annotation { "Feature Type Name" : "Feature", "Feature Type Description" : "" }
export const myFeature = defineFeature(function(context is Context, id is Id, definition is map)
    precondition{}
    {
        {
            var Q0;
            Q0=qCreatedBy(makeId("Front.planeOp"),FACE);
            var sketch = newSketch(context, id + "F0", { "sketchPlane" : qUnion([Q0])});
            skLineSegment(sketch, "E0.bottom", {"start": v(0, 0) * mm, "end": v(12.7, 0) * mm, "construction": true});
            skLineSegment(sketch, "E0.top", {"start": v(0, 38.1) * mm, "end": v(12.7, 38.1) * mm, "construction": true});
            skLineSegment(sketch, "E0.left", {"start": v(0, 0) * mm, "end": v(0, 38.1) * mm, "construction": true});
            skLineSegment(sketch, "E0.right", {"start": v(12.7, 0) * mm, "end": v(12.7, 38.1) * mm, "construction": true});
            skLineSegment(sketch, "E1", {"start": v(0, 38.1) * mm, "end": v(0, 0) * mm});
            skLineSegment(sketch, "E2", {"start": v(0, 0) * mm, "end": v(12.7, 0) * mm});
            skLineSegment(sketch, "E3", {"start": v(12.7, 0) * mm, "end": v(12.7, 5.08) * mm});
            skLineSegment(sketch, "E4", {"start": v(0, 38.1) * mm, "end": v(6.98, 38.1) * mm});
            skLineSegment(sketch, "E5", {"start": v(6.98, 38.1) * mm, "end": v(7.94, 33.02) * mm});
            skArc(sketch, "E6", {"start": v(7.94, 33.02) * mm, "mid": v(3.06, 23.93) * mm, "end": v(2.54, 13.63) * mm});
            skArc(sketch, "E7", {"start": v(2.54, 13.63) * mm, "mid": v(6.06, 7.5) * mm, "end": v(12.7, 5.08) * mm});
            skSolve(sketch);
        }
        {
            var Q0;
            Q0=sQuery(id+"F0.wireOp",EDGE,"E2");
            var Q1;
            Q1=sQuery(id+"F0.wireOp",VERTEX,"E3.start");
            cPlane(context, id + "F1", {"entities" : qUnion([Q0, Q1]), "cplaneType" : CPlaneType.LINE_POINT, "offset" : 25.4 * mm, "width" : 152.4 * mm, "height" : 152.4 * mm});
        }
        {
            var Q0;
            Q0=makeQuery(id+"F0.imprint","IMPRINT",FACE,{"disambiguationData":[TD([[makeQuery(id+"F0.imprint","IMPRINT",EDGE,{"derivedFrom":sQuery(id+"F0.wireOp",EDGE,"E1")}),1.0]])]});
            var Q1;
            Q1=sQuery(id+"F0.wireOp",EDGE,"E1");
            revolve(context, id + "F2", {"entities" : qUnion([Q0]), "axis" : qUnion([Q1]), "revolveType" : RevolveType.FULL});
        }
        {
            var Q0;
            Q0=qCreatedBy(id+"F1.planeOp",FACE);
            var sketch = newSketch(context, id + "F3", { "sketchPlane" : qUnion([Q0])});
            skLineSegment(sketch, "E8.0", {"start": v(-12.7, 0) * mm, "end": v(12.7, 0) * mm});
            skLineSegment(sketch, "E9.0", {"start": v(-12.7, 5.08) * mm, "end": v(12.7, 5.08) * mm});
            skLineSegment(sketch, "E10", {"start": v(12.7, 3.81) * mm, "end": v(12.7, 0) * mm});
            skText(sketch, "E11", { "text": "Kris Wagner", "fontName": "OpenSans-Bold.ttf"});
            skPoint(sketch, "E12", {"position": v(0, 5.08) * mm});
            const initialGuessF3  = {"E11": [-0.00837, 0.00154, 1, 0, 0.00199]};
            skSetInitialGuess(sketch, initialGuessF3);
            skSolve(sketch);
        }
        {
            var Q0;
            Q0 = qSketchRegion(id + "F3", true);
            var Q1;
            Q1=makeQuery(id+"F2.opRevolve","SWEPT_FACE",FACE,{"disambiguationData":[OSD([sQuery(id+"F0.wireOp",EDGE,"E3")])]});
            extrude(context, id + "F4", {"entities" : qUnion([Q0]), "operationType" : NewBodyOperationType.REMOVE, "endBound" : BoundingType.UP_TO_SURFACE, "oppositeDirection" : true, "depth" : 25.4 * mm, "endBoundEntityFace" : qUnion([Q1]), "hasOffset" : true, "offsetDistance" : 0.25 * mm, "offsetOppositeDirection" : true});
        }
        {
            var Q0;
            Q0=makeQuery(id+"F2.opRevolve","SWEPT_FACE",FACE,{"disambiguationData":[OSD([sQuery(id+"F0.wireOp",EDGE,"E4")])]});
            var sketch = newSketch(context, id + "F5", { "sketchPlane" : qUnion([Q0])});
            skArc(sketch, "E13.0", {"start": v(0, -7.94) * mm, "mid": v(0.7, -7.9) * mm, "end": v(1.38, -7.82) * mm});
            skCircle(sketch, "E14", {"center": v(0, 0) * mm, "radius": 5.08 * mm});
            skLineSegment(sketch, "E15", {"start": v(0, -5.08) * mm, "end": v(0, -7.94) * mm});
            skLineSegment(sketch, "E16", {"start": v(0.88, -5) * mm, "end": v(1.38, -7.82) * mm});
            skLineSegment(sketch, "E17.1.0", {"start": v(3.6, -3.6) * mm, "end": v(5.61, -5.61) * mm});
            skLineSegment(sketch, "E17.1.1", {"start": v(4.16, -2.91) * mm, "end": v(6.5, -4.55) * mm});
            skArc(sketch, "E17.1.2", {"start": v(5.61, -5.61) * mm, "mid": v(6.08, -5.1) * mm, "end": v(6.5, -4.55) * mm});
            skLineSegment(sketch, "E17.2.0", {"start": v(5.08, 0) * mm, "end": v(7.94, 0) * mm});
            skLineSegment(sketch, "E17.2.1", {"start": v(5, 0.88) * mm, "end": v(7.82, 1.38) * mm});
            skArc(sketch, "E17.2.2", {"start": v(7.94, 0) * mm, "mid": v(7.9, 0.7) * mm, "end": v(7.82, 1.38) * mm});
            skLineSegment(sketch, "E17.3.0", {"start": v(3.6, 3.6) * mm, "end": v(5.61, 5.61) * mm});
            skLineSegment(sketch, "E17.3.1", {"start": v(2.91, 4.16) * mm, "end": v(4.55, 6.5) * mm});
            skArc(sketch, "E17.3.2", {"start": v(5.61, 5.61) * mm, "mid": v(5.1, 6.08) * mm, "end": v(4.55, 6.5) * mm});
            skLineSegment(sketch, "E17.4.0", {"start": v(0, 5.08) * mm, "end": v(0, 7.94) * mm});
            skLineSegment(sketch, "E17.4.1", {"start": v(-0.88, 5) * mm, "end": v(-1.38, 7.82) * mm});
            skArc(sketch, "E17.4.2", {"start": v(0, 7.94) * mm, "mid": v(-0.7, 7.9) * mm, "end": v(-1.38, 7.82) * mm});
            skLineSegment(sketch, "E17.5.0", {"start": v(-3.6, 3.6) * mm, "end": v(-5.61, 5.61) * mm});
            skLineSegment(sketch, "E17.5.1", {"start": v(-4.16, 2.91) * mm, "end": v(-6.5, 4.55) * mm});
            skArc(sketch, "E17.5.2", {"start": v(-5.61, 5.61) * mm, "mid": v(-6.08, 5.1) * mm, "end": v(-6.5, 4.55) * mm});
            skLineSegment(sketch, "E17.6.0", {"start": v(-5.08, 0) * mm, "end": v(-7.94, 0) * mm});
            skLineSegment(sketch, "E17.6.1", {"start": v(-5, -0.88) * mm, "end": v(-7.82, -1.38) * mm});
            skArc(sketch, "E17.6.2", {"start": v(-7.94, 0) * mm, "mid": v(-7.9, -0.7) * mm, "end": v(-7.82, -1.38) * mm});
            skLineSegment(sketch, "E17.7.0", {"start": v(-3.6, -3.6) * mm, "end": v(-5.61, -5.61) * mm});
            skLineSegment(sketch, "E17.7.1", {"start": v(-2.91, -4.16) * mm, "end": v(-4.55, -6.5) * mm});
            skArc(sketch, "E17.7.2", {"start": v(-5.61, -5.61) * mm, "mid": v(-5.1, -6.08) * mm, "end": v(-4.55, -6.5) * mm});
            skSolve(sketch);
        }
        {
            var Q0;
            Q0 = qSketchRegion(id + "F5", true);
            extrude(context, id + "F6", {"entities" : qUnion([Q0]), "operationType" : NewBodyOperationType.REMOVE, "oppositeDirection" : true, "depth" : 5.08 * mm, "offsetDistance" : 25.4 * mm});
        }
    });